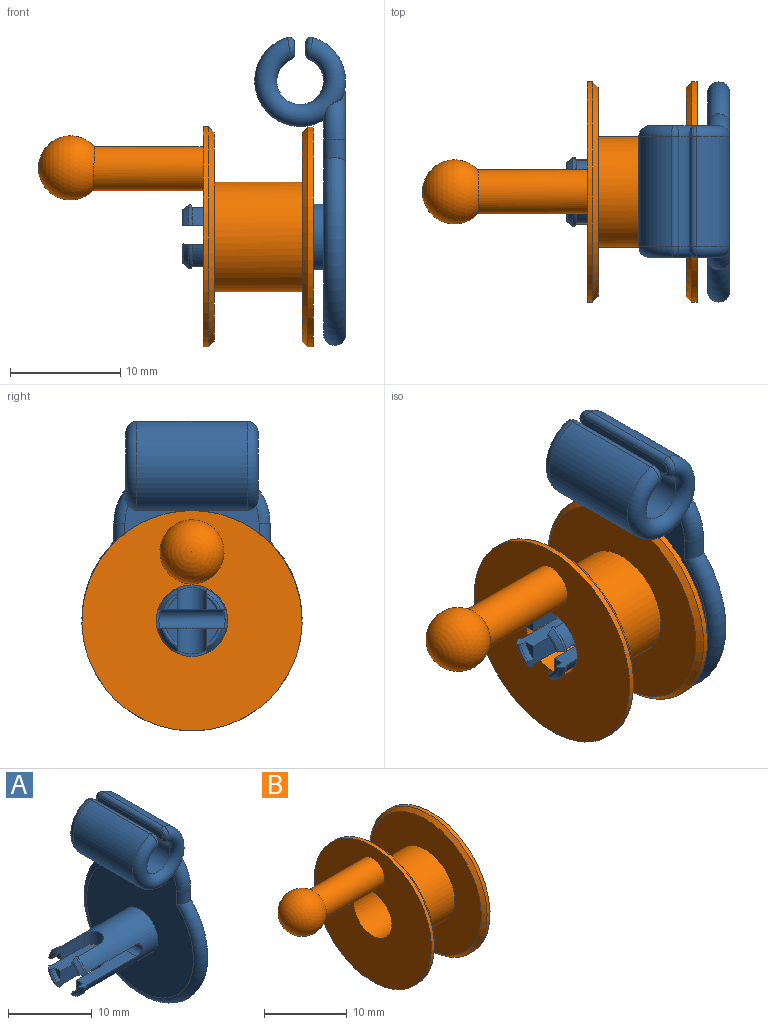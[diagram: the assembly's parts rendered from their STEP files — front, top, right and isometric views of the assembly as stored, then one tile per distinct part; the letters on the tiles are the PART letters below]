
ASSEMBLY  parts=2 mates=1
PART A: 52 faces, bbox 15.2x21.7x29.2 mm
  f0: torus R=3mm, axis (-1,0,0), area 1.3mm2, adj f1,f12,f19,f41
  f1: cone r=3.16mm half-angle=36.7deg, axis (1,0,0), area 1.5mm2, adj f0,f2,f12,f41
  f2: torus R=2.65mm, axis (-1,0,0), area 1mm2, adj f1,f3,f12,f41
  f3: cylinder r=2.45mm len=1.39mm, axis (-1,0,0), area 1.1mm2, adj f2,f4,f12,f41
  f4: plane 1.39x1.02mm, normal (-1,0,0), area 0.9mm2, adj f3,f12,f41
  f5: torus R=3mm, axis (-1,0,0), area 1.3mm2, adj f6,f11,f19,f41
  f6: cone r=3.16mm half-angle=36.7deg, axis (1,0,0), area 1.5mm2, adj f5,f7,f11,f41
  f7: torus R=2.65mm, axis (-1,0,0), area 1mm2, adj f6,f8,f11,f41
  f8: cylinder r=2.45mm len=1.39mm, axis (-1,0,0), area 1.1mm2, adj f7,f9,f11,f41
  f9: plane 1.39x1.02mm, normal (-1,0,0), area 0.9mm2, adj f8,f11,f41
  f10: cylinder r=1.34mm len=2.68mm, axis (0,0,1), area 9.1mm2, adj f11,f12,f19,f41
  f11: plane 4.78x2.29mm, normal (0,-1,0), area 8.4mm2, adj f5,f6,f7,f8,f9,f10,f19,f41
  f12: plane 4.78x2.29mm, normal (0,1,0), area 8.4mm2, adj f0,f1,f2,f3,f4,f10,f19,f41
  f13: torus R=3mm, axis (-1,0,0), area 1.1mm2, adj f14,f19,f38,f40
  f14: cone r=3.16mm half-angle=36.7deg, axis (1,0,0), area 1.3mm2, adj f13,f15,f38,f40
  f15: torus R=2.65mm, axis (-1,0,0), area 0.8mm2, adj f14,f16,f38,f40
  f16: cylinder r=2.45mm len=1.01mm, axis (-1,0,0), area 0.8mm2, adj f15,f17,f38,f40
  f17: plane 1.01x0.88mm, normal (-1,0,0), area 0.5mm2, adj f16,f38,f40
  f18: plane 21.76x18mm, normal (1,0,0), area 301.6mm2, adj f31,f32,f33,f34,f35
  f19: cylinder r=3mm len=11.95mm, axis (1,0,0), area 167.4mm2, adj f0,f5,f10,f11,f12,f13,f25,f26
  f20: cylinder r=4.12mm len=10mm, axis (0,-1,0), area 140.4mm2, adj f25,f42,f43,f44
  f21: cylinder r=4.12mm len=10mm, axis (0,-1,0), area 63.7mm2, adj f32,f34,f42,f43,f48
  f22: plane 11x1.06mm, normal (-1,0,0), area 11.4mm2, adj f48,f49,f50,f51
  f23: cylinder r=2.12mm len=10mm, axis (0,-1,0), area 116.9mm2, adj f42,f43,f47,f51
  f24: plane 11x1.06mm, normal (1,0,0), area 11.4mm2, adj f44,f45,f46,f47
  f25: plane 19.76x18.06mm, normal (-1,0,0), area 253mm2, adj f19,f20,f31,f32,f33,f34,f35,f42
  f26: torus R=3mm, axis (-1,0,0), area 1.1mm2, adj f19,f27,f37,f40
  f27: cone r=3.16mm half-angle=36.7deg, axis (1,0,0), area 1.3mm2, adj f26,f28,f37,f40
  f28: torus R=2.65mm, axis (-1,0,0), area 0.8mm2, adj f27,f29,f37,f40
  f29: cylinder r=2.45mm len=1.01mm, axis (-1,0,0), area 0.8mm2, adj f28,f30,f37,f40
  f30: plane 1.01x0.88mm, normal (-1,0,0), area 0.5mm2, adj f29,f37,f40
  f31: cylinder r=1mm len=2.13mm, axis (0,0,1), area 6mm2, adj f18,f25,f32,f33
  f32: torus R=4mm, axis (1,0,0), area 13.7mm2, adj f18,f21,f25,f31,f34,f43
  f33: torus R=9mm, axis (1,0,0), area 143.8mm2, adj f18,f25,f31,f35
  f34: torus R=4mm, axis (1,0,0), area 13.7mm2, adj f18,f21,f25,f32,f35,f42
  f35: cylinder r=1mm len=2.13mm, axis (0,0,-1), area 6mm2, adj f18,f25,f33,f34
  f36: cylinder r=1.34mm len=2.68mm, axis (0,0,1), area 6.9mm2, adj f19,f37,f38,f40
  f37: plane 4.78x1.92mm, normal (0,-1,0), area 7mm2, adj f19,f26,f27,f28,f29,f30,f36,f40
  f38: plane 4.78x1.92mm, normal (0,1,0), area 7mm2, adj f13,f14,f15,f16,f17,f19,f36,f40
  f39: cylinder r=0.85mm len=5.85mm, axis (0,-1,0), area 15.4mm2, adj f19,f40,f41
  f40: plane 9.39x6.09mm, normal (0,0,-1), area 35.8mm2, adj f13,f14,f15,f16,f17,f19,f26,f27
  f41: plane 9.38x6.28mm, normal (0,0,1), area 37.6mm2, adj f0,f1,f2,f3,f4,f5,f6,f7
  f42: torus R=3.12mm, axis (0,-1,0), area 53mm2, adj f20,f21,f23,f25,f34,f46,f50
  f43: torus R=3.12mm, axis (0,-1,0), area 53mm2, adj f20,f21,f23,f25,f32,f45,f49
  f44: cylinder r=0.5mm len=10mm, axis (0,-1,0), area 9.3mm2, adj f20,f24,f45,f46
  f45: bspline ~2.18x1.27mm, area 2mm2, adj f24,f43,f44,f47
  f46: bspline ~2.18x1.27mm, area 2mm2, adj f24,f42,f44,f47
  f47: cylinder r=0.5mm len=10mm, axis (0,-1,0), area 5.9mm2, adj f23,f24,f45,f46
  f48: cylinder r=0.5mm len=10mm, axis (0,-1,0), area 9.3mm2, adj f21,f22,f49,f50
  f49: bspline ~2.18x1.27mm, area 2mm2, adj f22,f43,f48,f51
  f50: bspline ~2.18x1.27mm, area 2mm2, adj f22,f42,f48,f51
  f51: cylinder r=0.5mm len=10mm, axis (0,-1,0), area 5.9mm2, adj f22,f23,f49,f50
PART B: 12 faces, bbox 25x20x20 mm
  f0: cylinder r=5mm len=10mm, axis (1,0,0), area 251.3mm2, adj f5,f6
  f1: cylinder r=3.25mm len=10mm, axis (1,0,0), area 204.2mm2, adj f2,f3
  f2: plane 20x20mm, normal (-1,0,0), area 268.4mm2, adj f1,f7,f10
  f3: plane 20x20mm, normal (1,0,0), area 281mm2, adj f1,f4
  f4: cylinder r=10mm len=20mm, axis (1,0,0), area 31.4mm2, adj f3,f9
  f5: plane 19x19mm, normal (-1,0,0), area 205mm2, adj f0,f9
  f6: plane 19x19mm, normal (1,0,0), area 205mm2, adj f0,f8
  f7: cylinder r=10mm len=20mm, axis (-1,0,0), area 31.4mm2, adj f2,f8
  f8: cone r=10mm half-angle=45deg, axis (-1,0,0), area 43.3mm2, adj f6,f7
  f9: cone r=10mm half-angle=45deg, axis (1,0,0), area 43.3mm2, adj f4,f5
  f10: cylinder r=2mm len=9.98mm, axis (1,0,0), area 124.6mm2, adj f2,f11
  f11: sphere r=2.91mm, area 92.2mm2, adj f10
PLACE A t=(-12.87,-7.17,1.04)mm
PLACE B t=(-12.62,-7.17,4.77)mm
MATE revolute B.f4 <-> A.f3  axis (-1,0,0) through (-34.01,-7.17,17.41)mm
